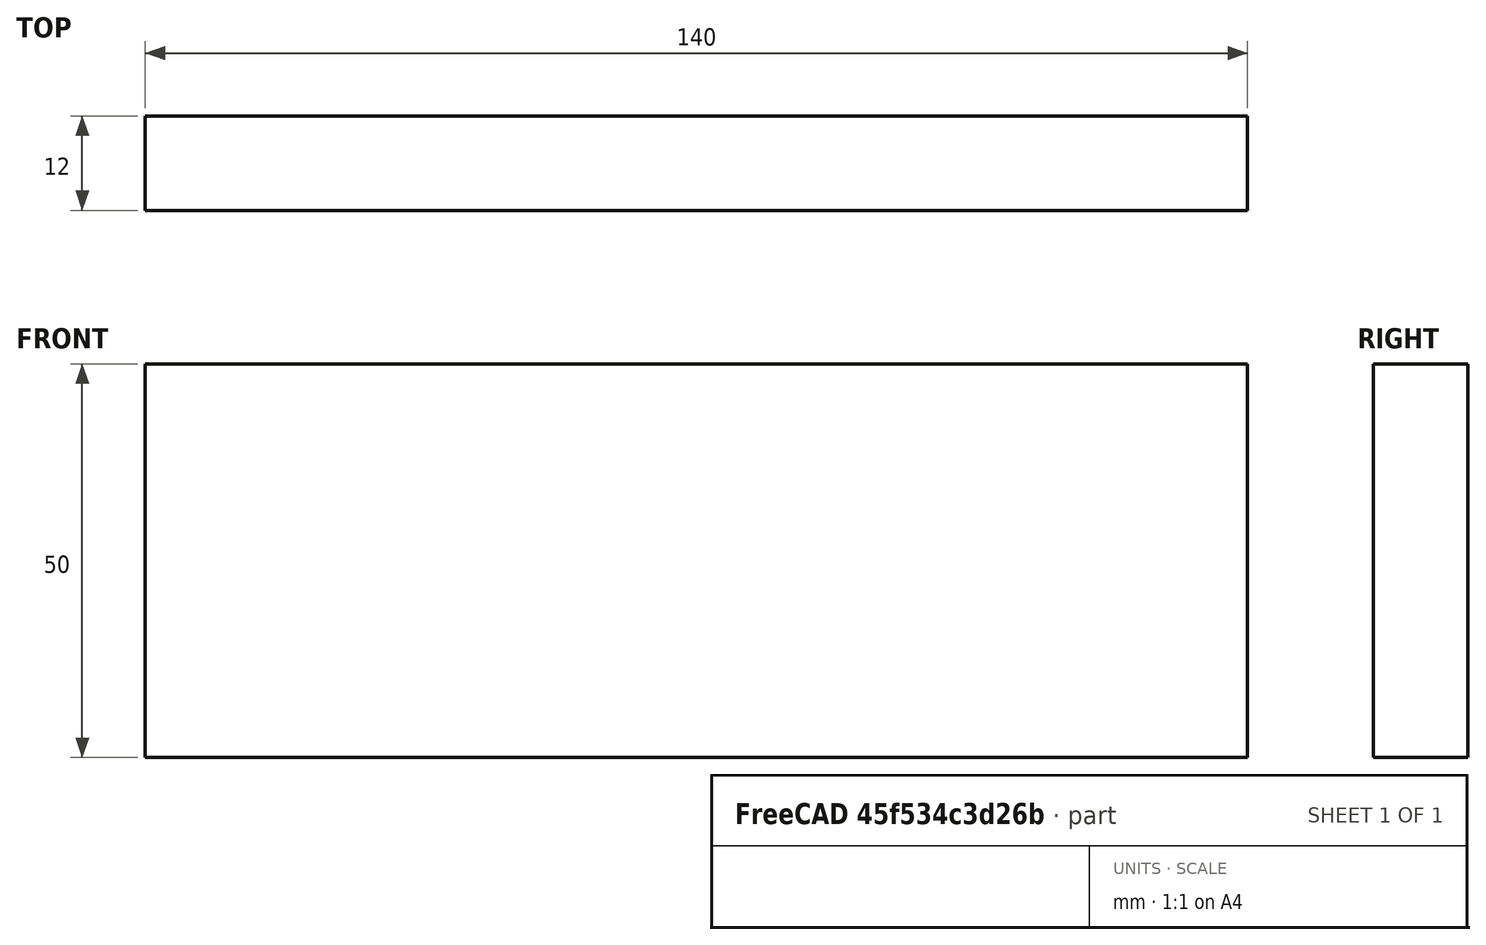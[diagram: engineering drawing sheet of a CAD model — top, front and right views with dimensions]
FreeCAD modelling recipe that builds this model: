
FCSTD DOCUMENT  (FreeCAD 0.15R4671 (Git))
Label: Flat Bar 140x12 EN10058 S235JR
License: All rights reserved
LicenseURL: http://en.wikipedia.org/wiki/All_rights_reserved
objects: Sketcher::SketchObject×1, Part::Extrusion×1
note: 2 computed .brp shape members not serialized (recipe doc carries the construction recipe); baked Part::Feature solids carry a one-line shape summary decoded from their .brp

FEATURE [Sketcher::SketchObject] Sketch
  sketch-geometry (4):
    g0: LineSegment StartX=-70 StartY=-6 StartZ=0 EndX=70 EndY=-6 EndZ=0
    g1: LineSegment StartX=70 StartY=-6 StartZ=0 EndX=70 EndY=6 EndZ=0
    g2: LineSegment StartX=70 StartY=6 StartZ=0 EndX=-70 EndY=6 EndZ=0
    g3: LineSegment StartX=-70 StartY=6 StartZ=0 EndX=-70 EndY=-6 EndZ=0
  constraints (12):
    c: Coincident(g0,g1)
    c: Coincident(g1,g2)
    c: Coincident(g2,g3)
    c: Coincident(g3,g0)
    c: Horizontal(g0)
    c: Horizontal(g2)
    c: Vertical(g1)
    c: Vertical(g3)
    c: Symmetric(g1,g2,g-2)
    c: Symmetric(g0,g1,g-1)
    c: DistanceY(g1) = 12
    c: DistanceX(g0) = 140
FEATURE [Part::Extrusion] Extrude  label="Flat Bar 140x12 EN10058 S235JR"
  Base = -> Sketch
  Dir = (0,0,50)
  Solid = true
